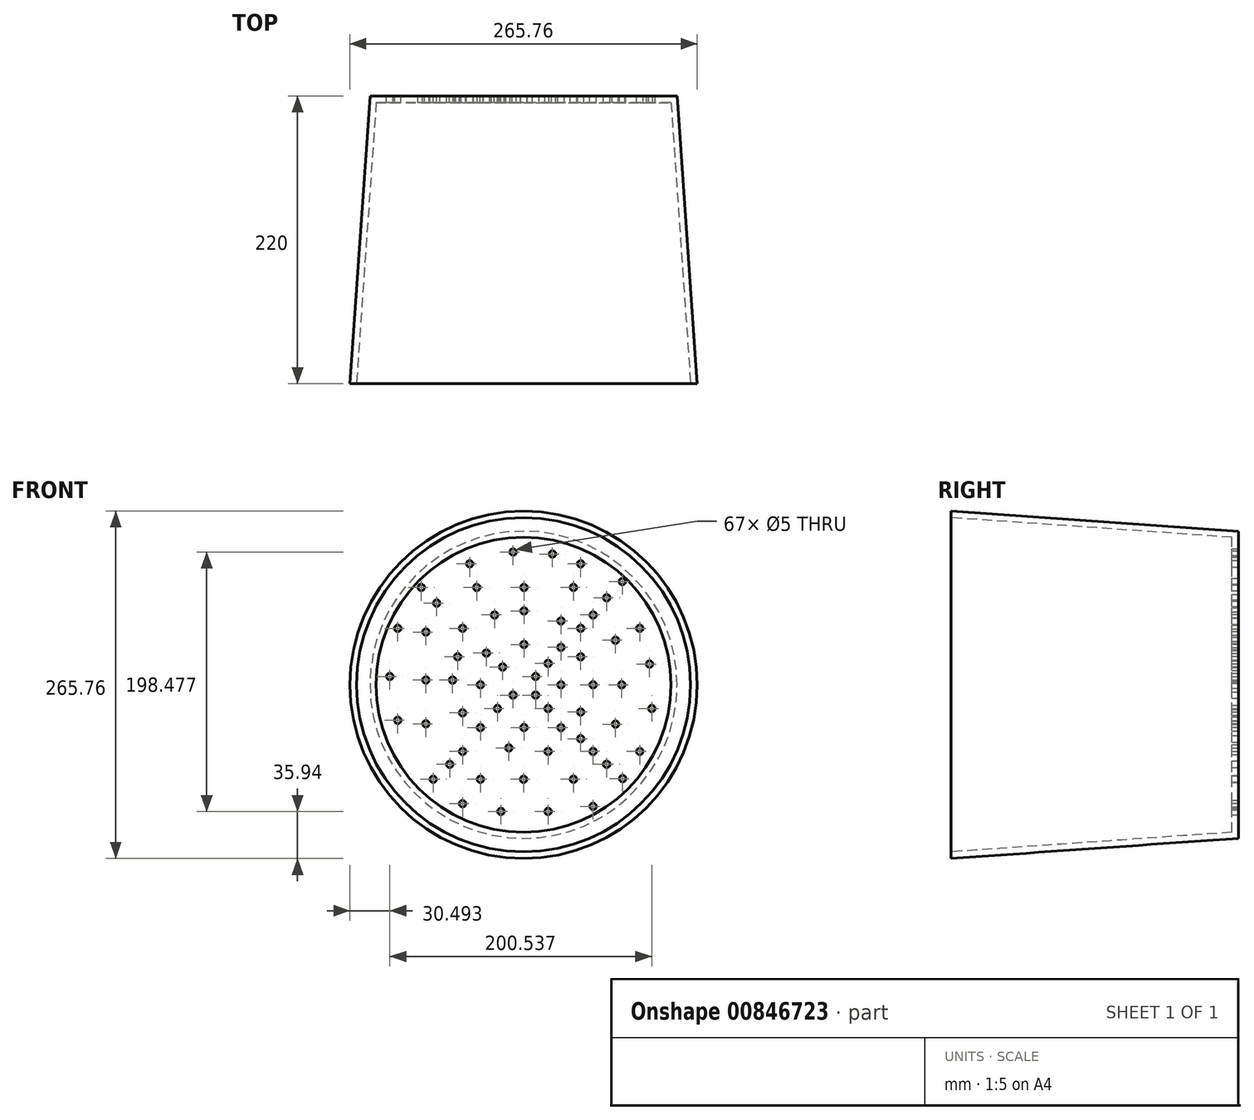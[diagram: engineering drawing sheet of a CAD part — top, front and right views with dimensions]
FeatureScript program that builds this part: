
annotation { "Feature Type Name" : "Feature", "Feature Type Description" : "" }
export const myFeature = defineFeature(function(context is Context, id is Id, definition is map)
    precondition{}
    {
        {
            var Q0;
            Q0=qCreatedBy(makeId("Front.planeOp"),FACE);
            var sketch = newSketch(context, id + "F0", { "sketchPlane" : qUnion([Q0])});
            skCircle(sketch, "E0", {"center": v(0, 0) * mm, "radius": 117.5 * mm});
            skPoint(sketch, "E1", {"position": v(0.36, 0) * mm});
            skPoint(sketch, "E2", {"position": v(-8, 6.35) * mm});
            skPoint(sketch, "E3", {"position": v(-16.02, 13.6) * mm});
            skPoint(sketch, "E4", {"position": v(-28.45, 24.23) * mm});
            skPoint(sketch, "E5", {"position": v(-46.66, 43.2) * mm});
            skPoint(sketch, "E6", {"position": v(-66.48, 62.46) * mm});
            skPoint(sketch, "E7", {"position": v(-78.28, 74.46) * mm});
            skPoint(sketch, "E8", {"position": v(9.2, -7.9) * mm});
            skPoint(sketch, "E9", {"position": v(18.8, -18.21) * mm});
            skPoint(sketch, "E10", {"position": v(28.67, -32.78) * mm});
            skPoint(sketch, "E11", {"position": v(43.75, -41.31) * mm});
            skPoint(sketch, "E12", {"position": v(53.21, -51.03) * mm});
            skPoint(sketch, "E13", {"position": v(63.63, -60.86) * mm});
            skPoint(sketch, "E14", {"position": v(75.83, -71.85) * mm});
            skPoint(sketch, "E15", {"position": v(9.2, 6.35) * mm});
            skPoint(sketch, "E16", {"position": v(18.8, 16.37) * mm});
            skPoint(sketch, "E17", {"position": v(28.67, 28.62) * mm});
            skPoint(sketch, "E18", {"position": v(43.75, 43.2) * mm});
            skPoint(sketch, "E19", {"position": v(53.21, 53.39) * mm});
            skPoint(sketch, "E20", {"position": v(63.63, 66.54) * mm});
            skPoint(sketch, "E21", {"position": v(75.66, 78.97) * mm});
            skPoint(sketch, "E22", {"position": v(-8, -7.9) * mm});
            skPoint(sketch, "E23", {"position": v(-19.96, -18.21) * mm});
            skPoint(sketch, "E24", {"position": v(-33.01, -32.78) * mm});
            skPoint(sketch, "E25", {"position": v(-41.2, -41.31) * mm});
            skPoint(sketch, "E26", {"position": v(-46.66, -51.03) * mm});
            skPoint(sketch, "E27", {"position": v(-56.49, -60.86) * mm});
            skPoint(sketch, "E28", {"position": v(-69.1, -72.3) * mm});
            skPoint(sketch, "E29", {"position": v(-78.28, -79.72) * mm});
            skPoint(sketch, "E30", {"position": v(-33.01, 0) * mm});
            skPoint(sketch, "E31", {"position": v(28.67, 0) * mm});
            skPoint(sketch, "E32", {"position": v(0.36, 30.84) * mm});
            skPoint(sketch, "E33", {"position": v(0.36, -32.78) * mm});
            skPoint(sketch, "E34", {"position": v(-46.66, -21.46) * mm});
            skPoint(sketch, "E35", {"position": v(-54.33, 3.64) * mm});
            skPoint(sketch, "E36", {"position": v(-50.38, 21.44) * mm});
            skPoint(sketch, "E37", {"position": v(-22.14, 53.39) * mm});
            skPoint(sketch, "E38", {"position": v(0.36, 56.47) * mm});
            skPoint(sketch, "E39", {"position": v(28.67, 48.82) * mm});
            skPoint(sketch, "E40", {"position": v(43.75, 21.44) * mm});
            skPoint(sketch, "E41", {"position": v(53.21, 0) * mm});
            skPoint(sketch, "E42", {"position": v(43.75, -20.87) * mm});
            skPoint(sketch, "E43", {"position": v(18.8, -51.03) * mm});
            skPoint(sketch, "E44", {"position": v(-11.23, -48.32) * mm});
            skPoint(sketch, "E45", {"position": v(0, -72.3) * mm});
            skPoint(sketch, "E46", {"position": v(-33.01, -72.3) * mm});
            skPoint(sketch, "E47", {"position": v(38.22, -72.3) * mm});
            skPoint(sketch, "E48", {"position": v(70.38, -30.12) * mm});
            skPoint(sketch, "E49", {"position": v(75.13, 0) * mm});
            skPoint(sketch, "E50", {"position": v(70.37, 34.04) * mm});
            skPoint(sketch, "E51", {"position": v(38.22, 74.46) * mm});
            skPoint(sketch, "E52", {"position": v(0.36, 74.46) * mm});
            skPoint(sketch, "E53", {"position": v(-35.84, 74.46) * mm});
            skPoint(sketch, "E54", {"position": v(-74.75, 40.34) * mm});
            skPoint(sketch, "E55", {"position": v(-74.75, 3.64) * mm});
            skPoint(sketch, "E56", {"position": v(-74.75, -29.85) * mm});
            skPoint(sketch, "E57", {"position": v(-96.25, -27.14) * mm});
            skPoint(sketch, "E58", {"position": v(-102.39, 6.35) * mm});
            skPoint(sketch, "E59", {"position": v(-96.25, 43.2) * mm});
            skPoint(sketch, "E60", {"position": v(-41.2, 92.56) * mm});
            skPoint(sketch, "E61", {"position": v(-8, 101.54) * mm});
            skPoint(sketch, "E62", {"position": v(22.14, 100.03) * mm});
            skPoint(sketch, "E63", {"position": v(43.75, 92.56) * mm});
            skPoint(sketch, "E64", {"position": v(88.9, 43.2) * mm});
            skPoint(sketch, "E65", {"position": v(96.44, 15.8) * mm});
            skPoint(sketch, "E66", {"position": v(98.15, -18.21) * mm});
            skPoint(sketch, "E67", {"position": v(88.9, -51.03) * mm});
            skPoint(sketch, "E68", {"position": v(53.21, -93.06) * mm});
            skPoint(sketch, "E69", {"position": v(18.8, -96.94) * mm});
            skPoint(sketch, "E70", {"position": v(-17.3, -96.94) * mm});
            skPoint(sketch, "E71", {"position": v(-46.66, -91) * mm});
            skSolve(sketch);
        }
        {
            var Q0;
            Q0=makeQuery(id+"F0.imprint","IMPRINT",FACE,{"disambiguationData":[TD([[makeQuery(id+"F0.imprint","IMPRINT",EDGE,{"derivedFrom":sQuery(id+"F0.wireOp",EDGE,"E0")}),1.0]])]});
            extrude(context, id + "F1", {"entities" : qUnion([Q0]), "depth" : 220 * mm, "offsetDistance" : 25.4 * mm, "hasDraft" : true, "draftAngle" : 4 * degree});
        }
        {
            var Q0;
            Q0=makeQuery(id+"F1.opExtrude","CAP_FACE",FACE,{"disambiguationData":[OSD([sQuery(id+"F0.wireOp",EDGE,"E0")])],"isStart":false});
            shell(context, id + "F2", {"entities" : qUnion([Q0]), "thickness" : 5 * mm});
        }
        {
            var Q0;
            Q0=sQuery(id+"F0.wireOp",VERTEX,"E15");
            var Q1;
            Q1=sQuery(id+"F0.wireOp",VERTEX,"E22");
            var Q2;
            Q2=sQuery(id+"F0.wireOp",VERTEX,"E8");
            var Q3;
            Q3=sQuery(id+"F0.wireOp",VERTEX,"E33");
            var Q4;
            Q4=sQuery(id+"F0.wireOp",VERTEX,"E9");
            var Q5;
            Q5=sQuery(id+"F0.wireOp",VERTEX,"E31");
            var Q6;
            Q6=sQuery(id+"F0.wireOp",VERTEX,"E16");
            var Q7;
            Q7=sQuery(id+"F0.wireOp",VERTEX,"E32");
            var Q8;
            Q8=sQuery(id+"F0.wireOp",VERTEX,"E3");
            var Q9;
            Q9=sQuery(id+"F0.wireOp",VERTEX,"E4");
            var Q10;
            Q10=sQuery(id+"F0.wireOp",VERTEX,"E30");
            var Q11;
            Q11=sQuery(id+"F0.wireOp",VERTEX,"E23");
            var Q12;
            Q12=sQuery(id+"F0.wireOp",VERTEX,"E10");
            var Q13;
            Q13=sQuery(id+"F0.wireOp",VERTEX,"E42");
            var Q14;
            Q14=sQuery(id+"F0.wireOp",VERTEX,"E41");
            var Q15;
            Q15=sQuery(id+"F0.wireOp",VERTEX,"E40");
            var Q16;
            Q16=sQuery(id+"F0.wireOp",VERTEX,"E17");
            var Q17;
            Q17=sQuery(id+"F0.wireOp",VERTEX,"E39");
            var Q18;
            Q18=sQuery(id+"F0.wireOp",VERTEX,"E38");
            var Q19;
            Q19=sQuery(id+"F0.wireOp",VERTEX,"E37");
            var Q20;
            Q20=sQuery(id+"F0.wireOp",VERTEX,"E5");
            var Q21;
            Q21=sQuery(id+"F0.wireOp",VERTEX,"E36");
            var Q22;
            Q22=sQuery(id+"F0.wireOp",VERTEX,"E35");
            var Q23;
            Q23=sQuery(id+"F0.wireOp",VERTEX,"E34");
            var Q24;
            Q24=sQuery(id+"F0.wireOp",VERTEX,"E24");
            var Q25;
            Q25=sQuery(id+"F0.wireOp",VERTEX,"E44");
            var Q26;
            Q26=sQuery(id+"F0.wireOp",VERTEX,"E43");
            var Q27;
            Q27=sQuery(id+"F0.wireOp",VERTEX,"E26");
            var Q28;
            Q28=sQuery(id+"F0.wireOp",VERTEX,"E27");
            var Q29;
            Q29=sQuery(id+"F0.wireOp",VERTEX,"E28");
            var Q30;
            Q30=sQuery(id+"F0.wireOp",VERTEX,"E11");
            var Q31;
            Q31=sQuery(id+"F0.wireOp",VERTEX,"E48");
            var Q32;
            Q32=sQuery(id+"F0.wireOp",VERTEX,"E49");
            var Q33;
            Q33=sQuery(id+"F0.wireOp",VERTEX,"E50");
            var Q34;
            Q34=sQuery(id+"F0.wireOp",VERTEX,"E18");
            var Q35;
            Q35=sQuery(id+"F0.wireOp",VERTEX,"E19");
            var Q36;
            Q36=sQuery(id+"F0.wireOp",VERTEX,"E51");
            var Q37;
            Q37=sQuery(id+"F0.wireOp",VERTEX,"E52");
            var Q38;
            Q38=sQuery(id+"F0.wireOp",VERTEX,"E53");
            var Q39;
            Q39=sQuery(id+"F0.wireOp",VERTEX,"E6");
            var Q40;
            Q40=sQuery(id+"F0.wireOp",VERTEX,"E54");
            var Q41;
            Q41=sQuery(id+"F0.wireOp",VERTEX,"E55");
            var Q42;
            Q42=sQuery(id+"F0.wireOp",VERTEX,"E56");
            var Q43;
            Q43=sQuery(id+"F0.wireOp",VERTEX,"E46");
            var Q44;
            Q44=sQuery(id+"F0.wireOp",VERTEX,"E71");
            var Q45;
            Q45=sQuery(id+"F0.wireOp",VERTEX,"E70");
            var Q46;
            Q46=sQuery(id+"F0.wireOp",VERTEX,"E45");
            var Q47;
            Q47=sQuery(id+"F0.wireOp",VERTEX,"E69");
            var Q48;
            Q48=sQuery(id+"F0.wireOp",VERTEX,"E47");
            var Q49;
            Q49=sQuery(id+"F0.wireOp",VERTEX,"E68");
            var Q50;
            Q50=sQuery(id+"F0.wireOp",VERTEX,"E14");
            var Q51;
            Q51=sQuery(id+"F0.wireOp",VERTEX,"E13");
            var Q52;
            Q52=sQuery(id+"F0.wireOp",VERTEX,"E12");
            var Q53;
            Q53=sQuery(id+"F0.wireOp",VERTEX,"E67");
            var Q54;
            Q54=sQuery(id+"F0.wireOp",VERTEX,"E66");
            var Q55;
            Q55=sQuery(id+"F0.wireOp",VERTEX,"E65");
            var Q56;
            Q56=sQuery(id+"F0.wireOp",VERTEX,"E64");
            var Q57;
            Q57=sQuery(id+"F0.wireOp",VERTEX,"E21");
            var Q58;
            Q58=sQuery(id+"F0.wireOp",VERTEX,"E20");
            var Q59;
            Q59=sQuery(id+"F0.wireOp",VERTEX,"E63");
            var Q60;
            Q60=sQuery(id+"F0.wireOp",VERTEX,"E62");
            var Q61;
            Q61=sQuery(id+"F0.wireOp",VERTEX,"E61");
            var Q62;
            Q62=sQuery(id+"F0.wireOp",VERTEX,"E60");
            var Q63;
            Q63=sQuery(id+"F0.wireOp",VERTEX,"E7");
            var Q64;
            Q64=sQuery(id+"F0.wireOp",VERTEX,"E59");
            var Q65;
            Q65=sQuery(id+"F0.wireOp",VERTEX,"E58");
            var Q66;
            Q66=sQuery(id+"F0.wireOp",VERTEX,"E57");
            var Q67;
            Q67=makeQuery(id+"F1.opExtrude","SWEPT_BODY",BODY,{"disambiguationData":[OSD([sQuery(id+"F0.wireOp",EDGE,"E0")])]});
            hole(context, id + "F3", {"style" : HoleStyle.SIMPLE, "endStyle" : HoleEndStyle.BLIND, "oppositeDirection" : true, "holeDiameter" : 5 * mm, "majorDiameter" : 6.35 * mm, "holeDepth" : 200 * mm, "isTappedThrough" : true, "tappedDepth" : 12.7 * mm, "tapClearance" : 3, "locations" : qUnion([Q0, Q1, Q2, Q3, Q4, Q5, Q6, Q7, Q8, Q9, Q10, Q11, Q12, Q13, Q14, Q15, Q16, Q17, Q18, Q19, Q20, Q21, Q22, Q23, Q24, Q25, Q26, Q27, Q28, Q29, Q30, Q31, Q32, Q33, Q34, Q35, Q36, Q37, Q38, Q39, Q40, Q41, Q42, Q43, Q44, Q45, Q46, Q47, Q48, Q49, Q50, Q51, Q52, Q53, Q54, Q55, Q56, Q57, Q58, Q59, Q60, Q61, Q62, Q63, Q64, Q65, Q66]), "scope" : qUnion([Q67])});
        }
    });
